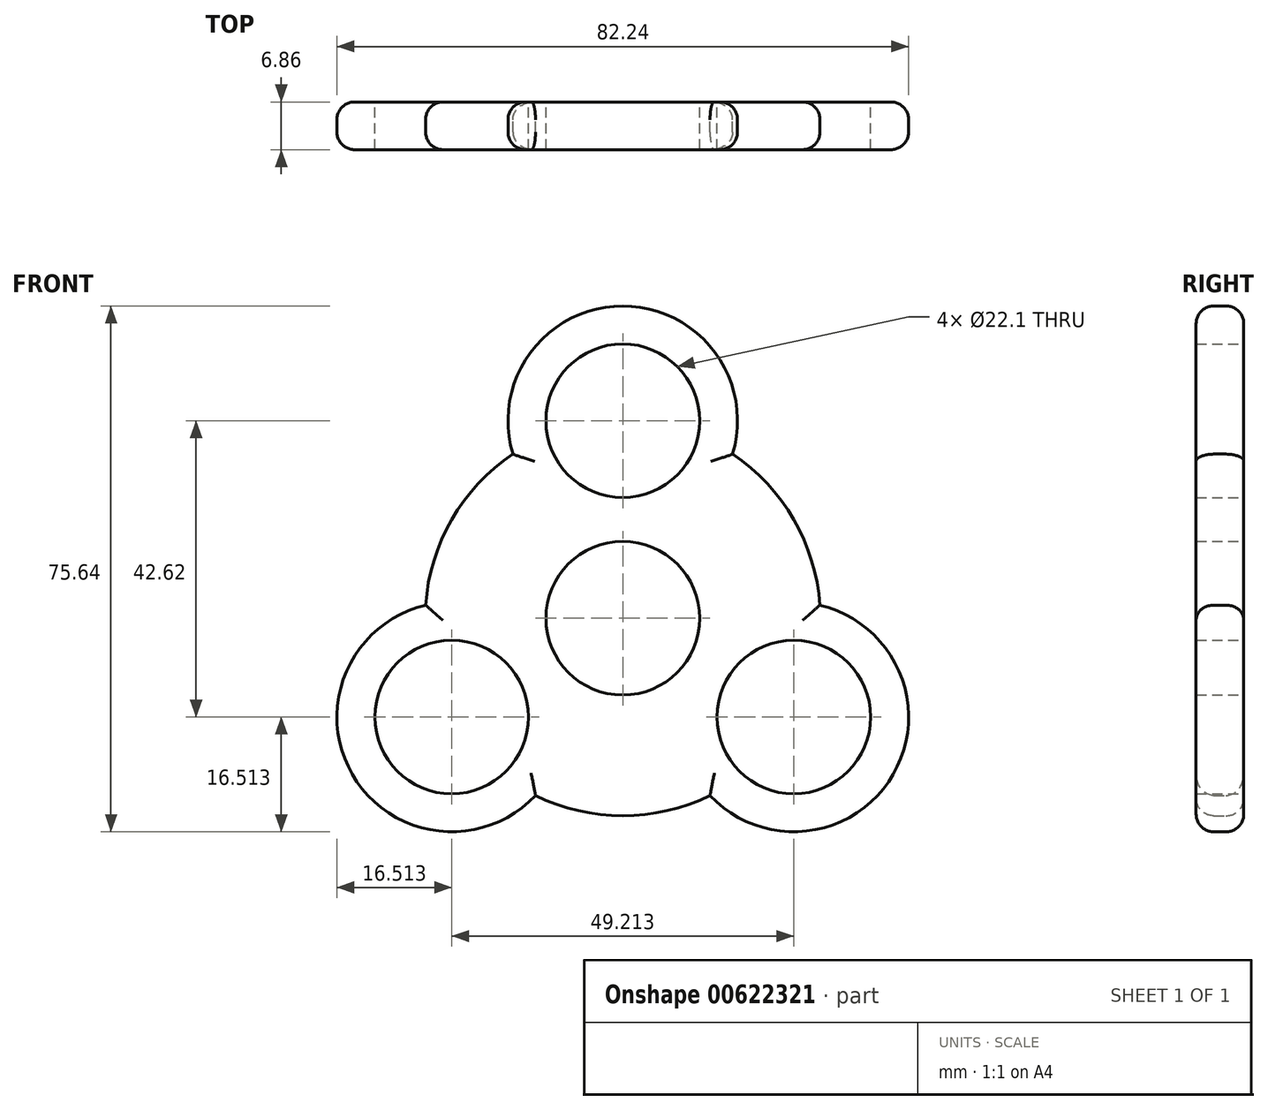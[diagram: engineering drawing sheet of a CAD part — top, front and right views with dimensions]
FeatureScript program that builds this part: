
annotation { "Feature Type Name" : "Feature", "Feature Type Description" : "" }
export const myFeature = defineFeature(function(context is Context, id is Id, definition is map)
    precondition{}
    {
        {
            var Q0;
            Q0=qCreatedBy(makeId("Front.planeOp"),FACE);
            var sketch = newSketch(context, id + "F0", { "sketchPlane" : qUnion([Q0])});
            skCircle(sketch, "E0", {"center": v(0, 0) * mm, "radius": 11.05 * mm});
            skCircle(sketch, "E1.1.1", {"center": v(-24.6, -14.2) * mm, "radius": 11.05 * mm});
            skCircle(sketch, "E1.2.1", {"center": v(24.6, -14.2) * mm, "radius": 11.05 * mm});
            skArc(sketch, "E2", {"start": v(-15.8, 23.62) * mm, "mid": v(-24.6, 14.2) * mm, "end": v(-28.35, 1.87) * mm});
            skArc(sketch, "E3", {"start": v(8.67, 21.56) * mm, "mid": v(2.6, 39.15) * mm, "end": v(-10.84, 26.27) * mm});
            skArc(sketch, "E4", {"start": v(-10.84, 26.27) * mm, "mid": v(-2.6, 17.67) * mm, "end": v(8.67, 21.56) * mm});
            skArc(sketch, "E5", {"start": v(15.8, 23.62) * mm, "mid": v(0, 44.92) * mm, "end": v(-15.8, 23.62) * mm});
            skArc(sketch, "E6", {"start": v(-28.35, 1.87) * mm, "mid": v(-38.9, -22.46) * mm, "end": v(-12.55, -25.49) * mm});
            skArc(sketch, "E7", {"start": v(12.55, -25.49) * mm, "mid": v(38.9, -22.46) * mm, "end": v(28.35, 1.87) * mm});
            skArc(sketch, "E8.trimOffspring", {"start": v(28.35, 1.87) * mm, "mid": v(24.6, 14.2) * mm, "end": v(15.8, 23.62) * mm});
            skArc(sketch, "E9.trimOffspring", {"start": v(-12.55, -25.49) * mm, "mid": v(0, -28.41) * mm, "end": v(12.55, -25.49) * mm});
            skSolve(sketch);
        }
        {
            var Q0;
            Q0=makeQuery(id+"F0.imprint","IMPRINT",FACE,{"disambiguationData":[TD([[makeQuery(id+"F0.imprint","IMPRINT",EDGE,{"derivedFrom":sQuery(id+"F0.wireOp",EDGE,"E1.1.1")}),-1.0]])]});
            extrude(context, id + "F1", {"entities" : qUnion([Q0]), "depth" : 6.86 * mm, "offsetDistance" : 25.4 * mm});
        }
        {
            var Q0;
            Q0=makeQuery(id+"F1.opExtrude","CAP_EDGE",EDGE,{"disambiguationData":[OSD([sQuery(id+"F0.wireOp",EDGE,"E8.trimOffspring")])],"isStart":false});
            var Q1;
            Q1=makeQuery(id+"F1.opExtrude","CAP_EDGE",EDGE,{"disambiguationData":[OSD([sQuery(id+"F0.wireOp",EDGE,"E5")])],"isStart":false});
            var Q2;
            Q2=makeQuery(id+"F1.opExtrude","CAP_EDGE",EDGE,{"disambiguationData":[OSD([sQuery(id+"F0.wireOp",EDGE,"E6")])],"isStart":false});
            var Q3;
            Q3=makeQuery(id+"F1.opExtrude","CAP_EDGE",EDGE,{"disambiguationData":[OSD([sQuery(id+"F0.wireOp",EDGE,"E2")])],"isStart":false});
            var Q4;
            Q4=makeQuery(id+"F1.opExtrude","CAP_EDGE",EDGE,{"disambiguationData":[OSD([sQuery(id+"F0.wireOp",EDGE,"E9.trimOffspring")])],"isStart":false});
            var Q5;
            Q5=makeQuery(id+"F1.opExtrude","CAP_EDGE",EDGE,{"disambiguationData":[OSD([sQuery(id+"F0.wireOp",EDGE,"E7")])],"isStart":false});
            var Q6;
            Q6=makeQuery(id+"F1.opExtrude","CAP_EDGE",EDGE,{"disambiguationData":[OSD([sQuery(id+"F0.wireOp",EDGE,"E5")])],"isStart":true});
            var Q7;
            Q7=makeQuery(id+"F1.opExtrude","CAP_EDGE",EDGE,{"disambiguationData":[OSD([sQuery(id+"F0.wireOp",EDGE,"E2")])],"isStart":true});
            var Q8;
            Q8=makeQuery(id+"F1.opExtrude","CAP_EDGE",EDGE,{"disambiguationData":[OSD([sQuery(id+"F0.wireOp",EDGE,"E6")])],"isStart":true});
            var Q9;
            Q9=makeQuery(id+"F1.opExtrude","CAP_EDGE",EDGE,{"disambiguationData":[OSD([sQuery(id+"F0.wireOp",EDGE,"E9.trimOffspring")])],"isStart":true});
            var Q10;
            Q10=makeQuery(id+"F1.opExtrude","CAP_EDGE",EDGE,{"disambiguationData":[OSD([sQuery(id+"F0.wireOp",EDGE,"E7")])],"isStart":true});
            var Q11;
            Q11=makeQuery(id+"F1.opExtrude","CAP_EDGE",EDGE,{"disambiguationData":[OSD([sQuery(id+"F0.wireOp",EDGE,"E8.trimOffspring")])],"isStart":true});
            fillet(context, id + "F2", {"entities" : qUnion([Q0, Q1, Q2, Q3, Q4, Q5, Q6, Q7, Q8, Q9, Q10, Q11]), "radius" : 2.54 * mm, "tangentPropagation" : true, "allowEdgeOverflow" : false});
        }
    });
